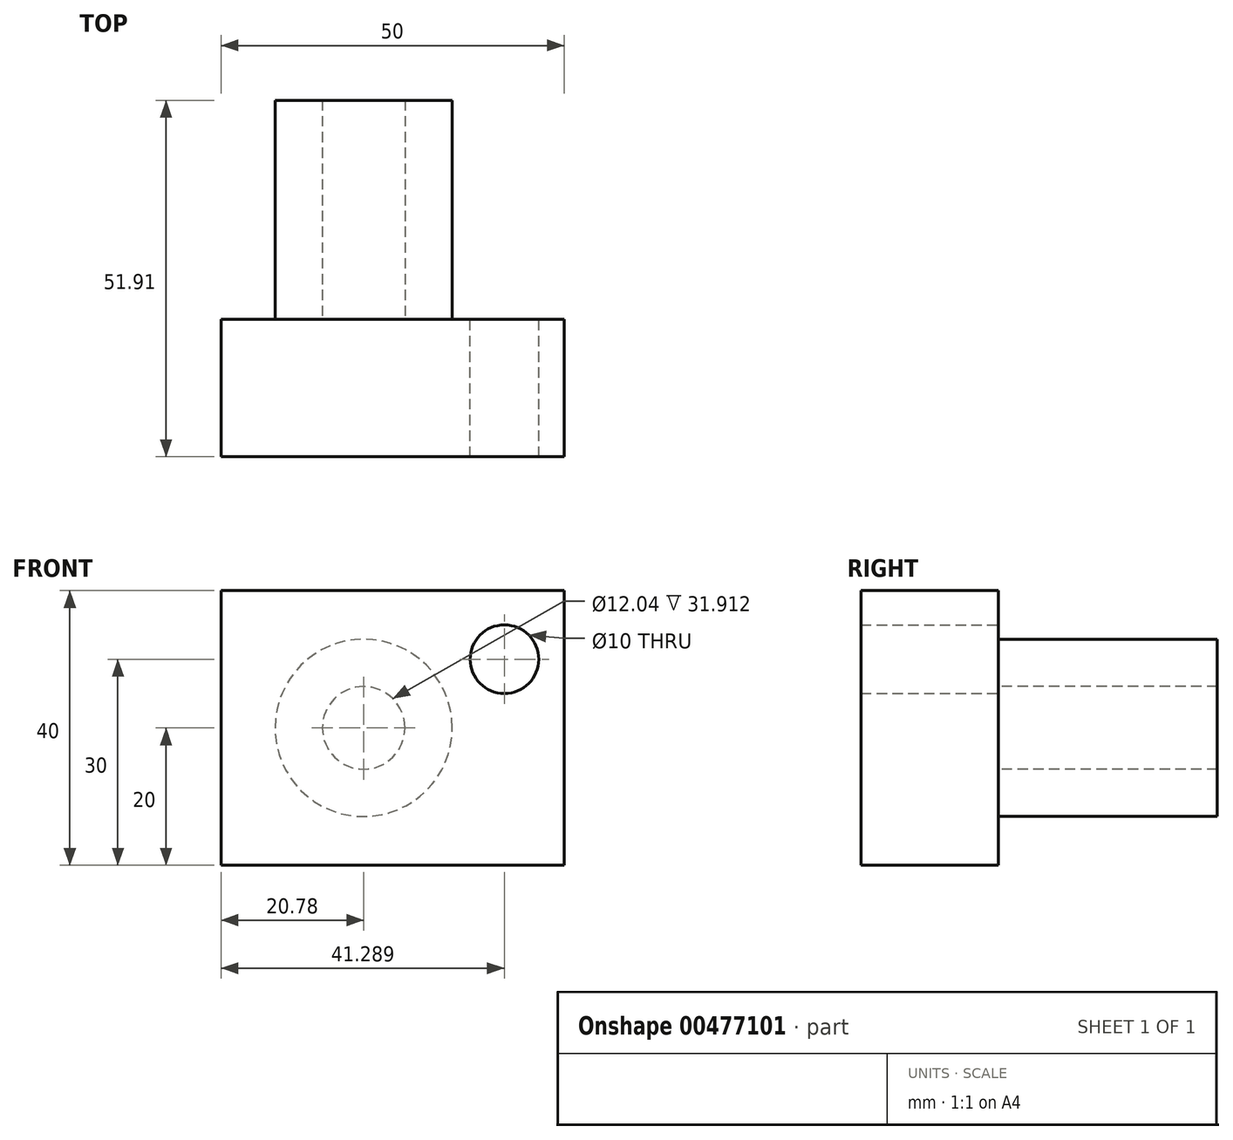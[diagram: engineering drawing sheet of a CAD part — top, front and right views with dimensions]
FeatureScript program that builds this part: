
annotation { "Feature Type Name" : "Feature", "Feature Type Description" : "" }
export const myFeature = defineFeature(function(context is Context, id is Id, definition is map)
    precondition{}
    {
        {
            var Q0;
            Q0=qCreatedBy(makeId("Front.planeOp"),FACE);
            var sketch = newSketch(context, id + "F0", { "sketchPlane" : qUnion([Q0])});
            skLineSegment(sketch, "E0", {"start": v(-20.78, 0) * mm, "end": v(-20.78, 20) * mm});
            skLineSegment(sketch, "E1", {"start": v(-20.78, 20) * mm, "end": v(29.22, 20) * mm});
            skLineSegment(sketch, "E2", {"start": v(29.22, 20) * mm, "end": v(29.22, -20) * mm});
            skLineSegment(sketch, "E3", {"start": v(29.22, -20) * mm, "end": v(-20.78, -20) * mm});
            skLineSegment(sketch, "E4", {"start": v(-20.78, -20) * mm, "end": v(-20.78, 0) * mm});
            skSolve(sketch);
        }
        {
            var Q0;
            Q0 = qSketchRegion(id + "F0", true);
            extrude(context, id + "F1", {"entities" : qUnion([Q0]), "depth" : 20 * mm});
        }
        {
            var Q0;
            Q0=qCreatedBy(makeId("Right.planeOp"),FACE);
            var sketch = newSketch(context, id + "F2", { "sketchPlane" : qUnion([Q0])});
            skLineSegment(sketch, "E5.bottom", {"start": v(0, 12.9) * mm, "end": v(31.91, 12.9) * mm});
            skLineSegment(sketch, "E5.top", {"start": v(0, 6.02) * mm, "end": v(31.91, 6.02) * mm});
            skLineSegment(sketch, "E5.left", {"start": v(0, 12.9) * mm, "end": v(0, 6.02) * mm});
            skLineSegment(sketch, "E5.right", {"start": v(31.91, 12.9) * mm, "end": v(31.91, 6.02) * mm});
            skLineSegment(sketch, "E6", {"start": v(0, 0) * mm, "end": v(31.91, 0) * mm, "construction": true});
            skSolve(sketch);
        }
        {
            var Q0;
            Q0 = qSketchRegion(id + "F2", true);
            var Q1;
            Q1=sQuery(id+"F2.wireOp",EDGE,"E6");
            revolve(context, id + "F3", {"operationType" : NewBodyOperationType.ADD, "entities" : qUnion([Q0]), "axis" : qUnion([Q1]), "revolveType" : RevolveType.FULL});
        }
        {
            var Q0;
            {var subQ0=sQuery(id+"F0.wireOp",EDGE,"E3");var subQ1=sQuery(id+"F0.wireOp",EDGE,"E2");var subQ2=sQuery(id+"F0.wireOp",EDGE,"E1");var subQ3=sQuery(id+"F0.wireOp",EDGE,"E4");var subQ4=sQuery(id+"F0.wireOp",EDGE,"E0");Q0=makeQuery(id+"F3.boolean.opBoolean","SPLIT",FACE,{"disambiguationData":[TD([makeQuery(id+"F1.opExtrude","SWEPT_FACE",FACE,{"disambiguationData":[OSD([subQ2])]})])],"derivedFrom":makeQuery(id+"F1.opExtrude","CAP_FACE",FACE,{"disambiguationData":[OSD([subQ4,subQ2,subQ1,subQ0,subQ3])],"isStart":true})});}
            var sketch = newSketch(context, id + "F4", { "sketchPlane" : qUnion([Q0])});
            skPoint(sketch, "E7", {"position": v(-20.5, 10) * mm});
            skSolve(sketch);
        }
        {
            var Q0;
            Q0=sQuery(id+"F4.wireOp",VERTEX,"E7");
            var Q1;
            Q1=makeQuery(id+"F1.opExtrude","SWEPT_BODY",BODY,{"disambiguationData":[OSD([sQuery(id+"F0.wireOp",EDGE,"E0"),sQuery(id+"F0.wireOp",EDGE,"E1"),sQuery(id+"F0.wireOp",EDGE,"E2"),sQuery(id+"F0.wireOp",EDGE,"E3"),sQuery(id+"F0.wireOp",EDGE,"E4")])]});
            hole(context, id + "F5", {"style" : HoleStyle.SIMPLE, "endStyle" : HoleEndStyle.THROUGH, "holeDiameter" : 10 * mm, "isTappedThrough" : true, "tappedDepth" : 12 * mm, "tapClearance" : 3, "locations" : qUnion([Q0]), "scope" : qUnion([Q1])});
        }
    });
